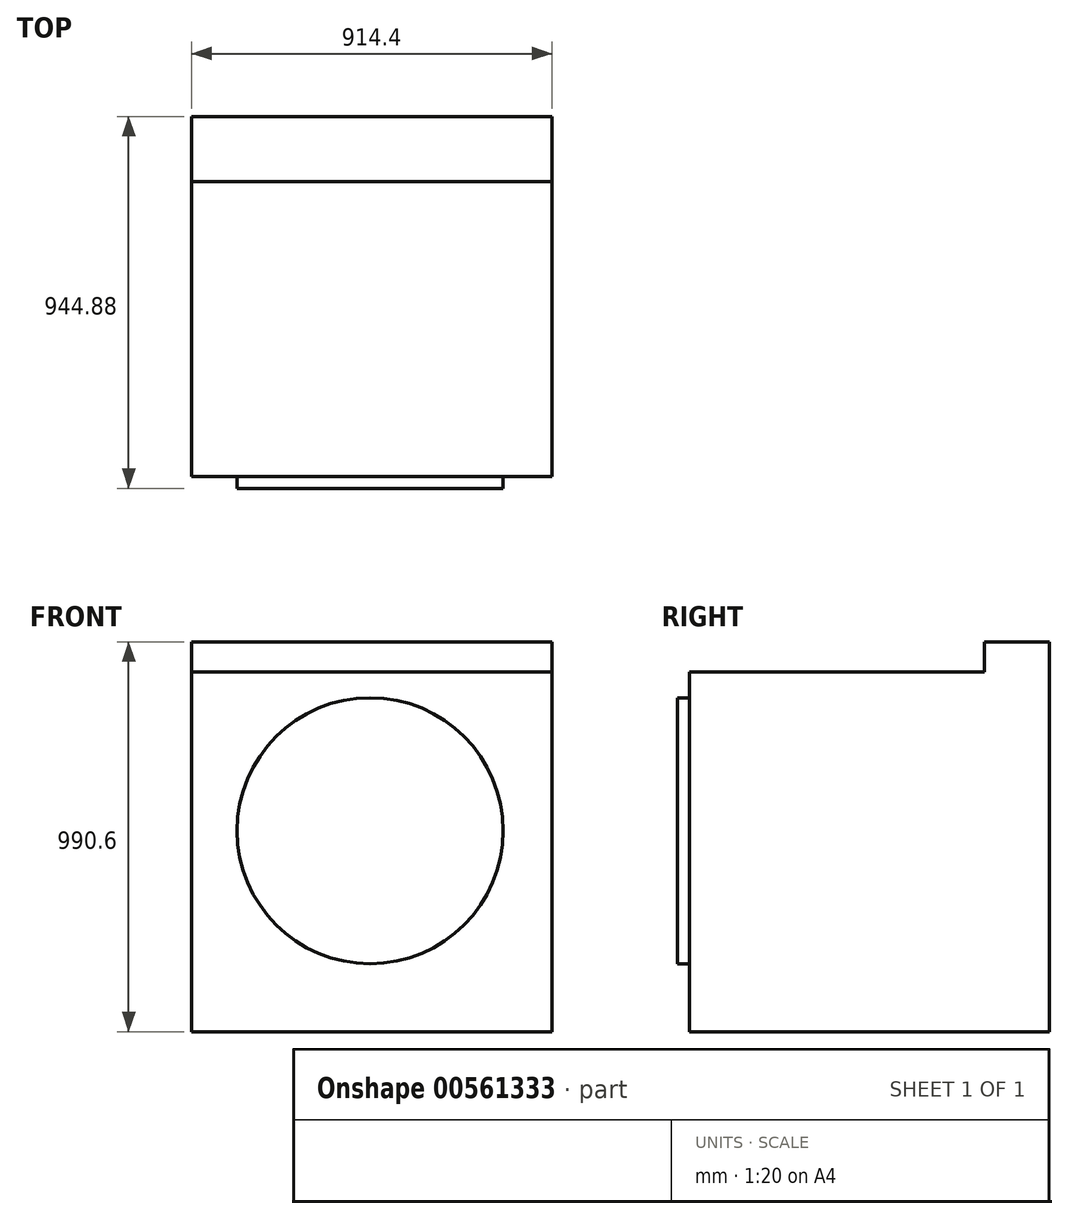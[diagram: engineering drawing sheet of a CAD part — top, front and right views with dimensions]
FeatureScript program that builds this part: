
annotation { "Feature Type Name" : "Feature", "Feature Type Description" : "" }
export const myFeature = defineFeature(function(context is Context, id is Id, definition is map)
    precondition{}
    {
        {
            var Q0;
            Q0=qCreatedBy(makeId("Top.planeOp"),FACE);
            var sketch = newSketch(context, id + "F0", { "sketchPlane" : qUnion([Q0])});
            skLineSegment(sketch, "E0.bottom", {"start": v(-453.03, 545.81) * mm, "end": v(461.37, 545.81) * mm});
            skLineSegment(sketch, "E0.top", {"start": v(-453.03, -368.59) * mm, "end": v(461.37, -368.59) * mm});
            skLineSegment(sketch, "E0.left", {"start": v(-453.03, 545.81) * mm, "end": v(-453.03, -368.59) * mm});
            skLineSegment(sketch, "E0.right", {"start": v(461.37, 545.81) * mm, "end": v(461.37, -368.59) * mm});
            skSolve(sketch);
        }
        {
            var Q0;
            Q0 = qSketchRegion(id + "F0", true);
            extrude(context, id + "F1", {"entities" : qUnion([Q0]), "depth" : 914.4 * mm, "offsetDistance" : 30.48 * mm});
        }
        {
            var Q0;
            Q0=makeQuery(id+"F1.opExtrude","CAP_FACE",FACE,{"disambiguationData":[OSD([sQuery(id+"F0.wireOp",EDGE,"E0.bottom"),sQuery(id+"F0.wireOp",EDGE,"E0.top"),sQuery(id+"F0.wireOp",EDGE,"E0.left"),sQuery(id+"F0.wireOp",EDGE,"E0.right")])],"isStart":false});
            var sketch = newSketch(context, id + "F2", { "sketchPlane" : qUnion([Q0])});
            skLineSegment(sketch, "E1.bottom", {"start": v(-453.03, 545.81) * mm, "end": v(461.37, 545.81) * mm});
            skLineSegment(sketch, "E1.top", {"start": v(-453.03, 380.1) * mm, "end": v(461.37, 380.1) * mm});
            skLineSegment(sketch, "E1.left", {"start": v(-453.03, 545.81) * mm, "end": v(-453.03, 380.1) * mm});
            skLineSegment(sketch, "E1.right", {"start": v(461.37, 545.81) * mm, "end": v(461.37, 380.1) * mm});
            skSolve(sketch);
        }
        {
            var Q0;
            Q0 = qSketchRegion(id + "F2", true);
            extrude(context, id + "F3", {"entities" : qUnion([Q0]), "operationType" : NewBodyOperationType.ADD, "depth" : 76.2 * mm, "offsetDistance" : 30.48 * mm});
        }
        {
            var Q0;
            Q0=makeQuery(id+"F1.opExtrude","SWEPT_FACE",FACE,{"disambiguationData":[OSD([sQuery(id+"F0.wireOp",EDGE,"E0.top")])]});
            var sketch = newSketch(context, id + "F4", { "sketchPlane" : qUnion([Q0])});
            skCircle(sketch, "E2", {"center": v(0, 510.47) * mm, "radius": 337.99 * mm});
            skSolve(sketch);
        }
        {
            var Q0;
            Q0 = qSketchRegion(id + "F4", true);
            extrude(context, id + "F5", {"entities" : qUnion([Q0]), "operationType" : NewBodyOperationType.ADD, "depth" : 30.48 * mm, "offsetDistance" : 30.48 * mm});
        }
    });
